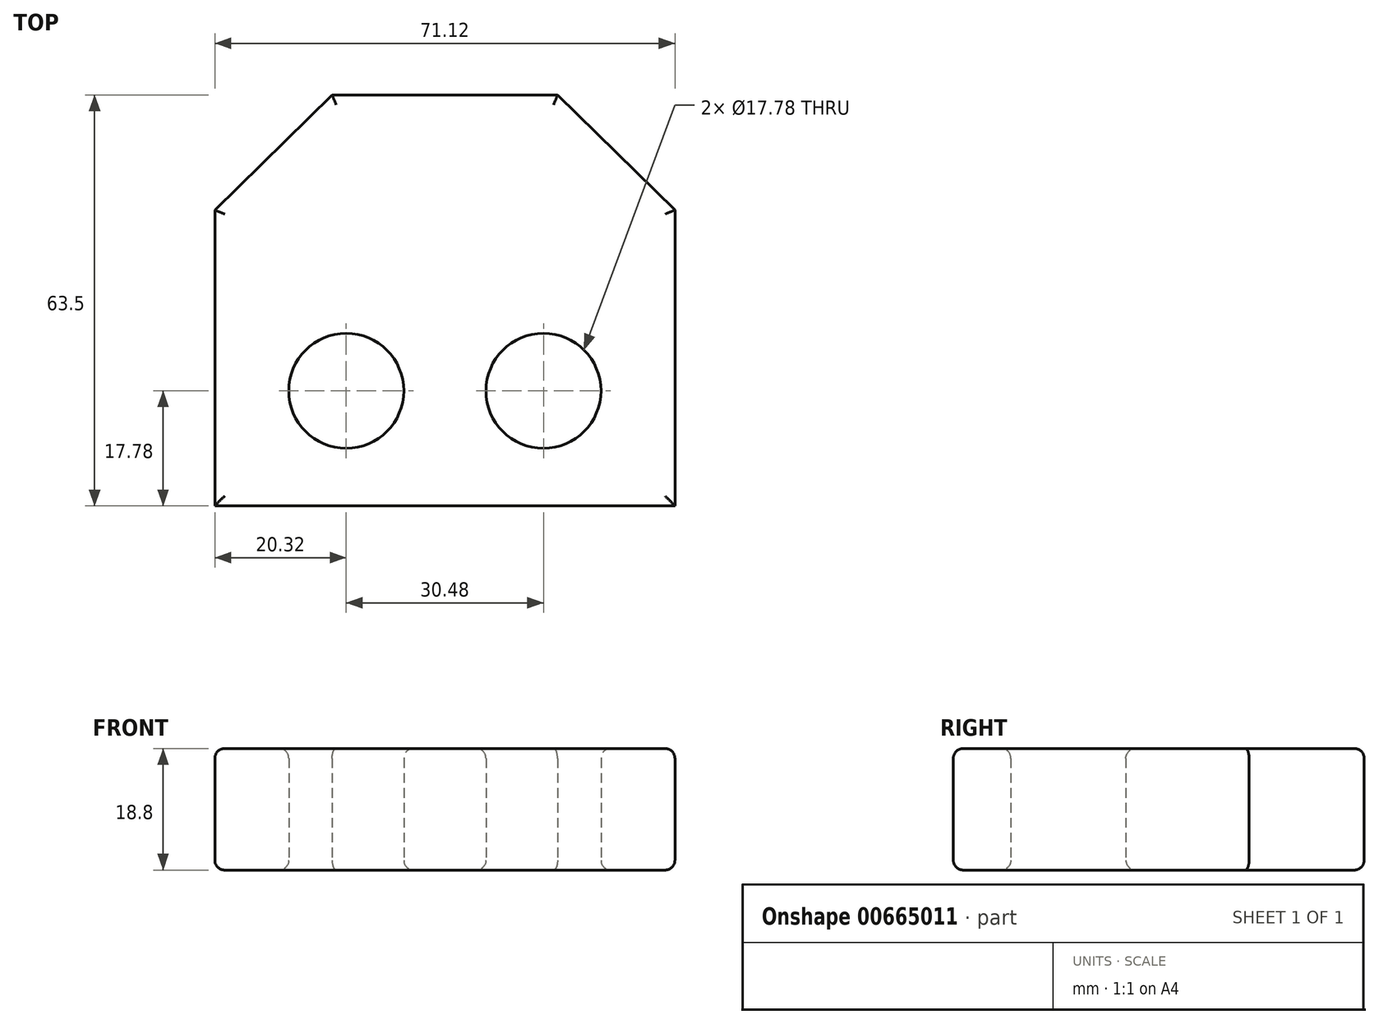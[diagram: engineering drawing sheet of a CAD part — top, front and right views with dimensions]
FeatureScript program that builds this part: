
annotation { "Feature Type Name" : "Feature", "Feature Type Description" : "" }
export const myFeature = defineFeature(function(context is Context, id is Id, definition is map)
    precondition{}
    {
        {
            var Q0;
            Q0=qCreatedBy(makeId("Top.planeOp"),FACE);
            var sketch = newSketch(context, id + "F0", { "sketchPlane" : qUnion([Q0])});
            skLineSegment(sketch, "E0", {"start": v(0, 0) * mm, "end": v(0, 45.72) * mm});
            skLineSegment(sketch, "E1", {"start": v(0, 45.72) * mm, "end": v(18.14, 63.5) * mm});
            skLineSegment(sketch, "E2", {"start": v(18.14, 63.5) * mm, "end": v(52.98, 63.5) * mm});
            skLineSegment(sketch, "E3", {"start": v(52.98, 63.5) * mm, "end": v(71.12, 45.72) * mm});
            skLineSegment(sketch, "E4", {"start": v(71.12, 45.72) * mm, "end": v(71.12, 0) * mm});
            skLineSegment(sketch, "E5", {"start": v(71.12, 0) * mm, "end": v(0, 0) * mm});
            skCircle(sketch, "E6", {"center": v(20.32, 17.78) * mm, "radius": 8.9 * mm});
            skCircle(sketch, "E7", {"center": v(50.8, 17.78) * mm, "radius": 8.9 * mm});
            skLineSegment(sketch, "E8", {"start": v(20.32, 17.78) * mm, "end": v(20.32, 0) * mm});
            skLineSegment(sketch, "E9", {"start": v(50.8, 17.78) * mm, "end": v(50.8, 0) * mm});
            skLineSegment(sketch, "E10", {"start": v(20.32, 17.78) * mm, "end": v(0, 17.78) * mm});
            skLineSegment(sketch, "E11", {"start": v(50.8, 17.78) * mm, "end": v(71.12, 17.78) * mm});
            skSolve(sketch);
        }
        {
            var Q0;
            {var subQ16=sQuery(id+"F0.wireOp",EDGE,"E1");Q0=makeQuery(id+"F0.imprint","IMPRINT",FACE,{"disambiguationData":[TD([[makeQuery(id+"F0.imprint","IMPRINT",EDGE,{"derivedFrom":subQ16}),-1.0]])]});}
            var Q1;
            {var subQ0=sQuery(id+"F0.wireOp",EDGE,"E5");var subQ1=sQuery(id+"F0.wireOp",EDGE,"E0");var subQ2=makeQuery(id+"F0.imprint","INTERSECT",VERTEX,{"derivedFrom":[subQ1,subQ0]});Q1=makeQuery(id+"F0.imprint","IMPRINT",FACE,{"disambiguationData":[TD([[makeQuery(id+"F0.imprint","IMPRINT",EDGE,{"disambiguationData":[TD([[subQ2,-1.0]])],"derivedFrom":subQ1}),-1.0]])]});}
            var Q2;
            {var subQ5=sQuery(id+"F0.wireOp",EDGE,"E5");var subQ7=sQuery(id+"F0.wireOp",EDGE,"E4");var subQ8=makeQuery(id+"F0.imprint","INTERSECT",VERTEX,{"derivedFrom":[subQ7,subQ5]});Q2=makeQuery(id+"F0.imprint","IMPRINT",FACE,{"disambiguationData":[TD([[makeQuery(id+"F0.imprint","IMPRINT",EDGE,{"disambiguationData":[TD([[subQ8,1.0]])],"derivedFrom":subQ7}),-1.0]])]});}
            extrude(context, id + "F1", {"entities" : qUnion([Q0, Q1, Q2]), "depth" : 18.8 * mm, "offsetDistance" : 25.4 * mm});
        }
        {
            var Q0;
            Q0=makeQuery(id+"F1.opExtrude","CAP_FACE",FACE,{"disambiguationData":[OSD([sQuery(id+"F0.wireOp",EDGE,"E0"),sQuery(id+"F0.wireOp",EDGE,"E1"),sQuery(id+"F0.wireOp",EDGE,"E2"),sQuery(id+"F0.wireOp",EDGE,"E3"),sQuery(id+"F0.wireOp",EDGE,"E4"),sQuery(id+"F0.wireOp",EDGE,"E5"),sQuery(id+"F0.wireOp",EDGE,"E6"),sQuery(id+"F0.wireOp",EDGE,"E7")])],"isStart":false});
            var Q1;
            Q1=makeQuery(id+"F1.opExtrude","CAP_FACE",FACE,{"disambiguationData":[OSD([sQuery(id+"F0.wireOp",EDGE,"E0"),sQuery(id+"F0.wireOp",EDGE,"E1"),sQuery(id+"F0.wireOp",EDGE,"E2"),sQuery(id+"F0.wireOp",EDGE,"E3"),sQuery(id+"F0.wireOp",EDGE,"E4"),sQuery(id+"F0.wireOp",EDGE,"E5"),sQuery(id+"F0.wireOp",EDGE,"E6"),sQuery(id+"F0.wireOp",EDGE,"E7")])],"isStart":true});
            fillet(context, id + "F2", {"entities" : qUnion([Q0, Q1]), "radius" : 1.52 * mm, "tangentPropagation" : true, "allowEdgeOverflow" : false});
        }
    });
